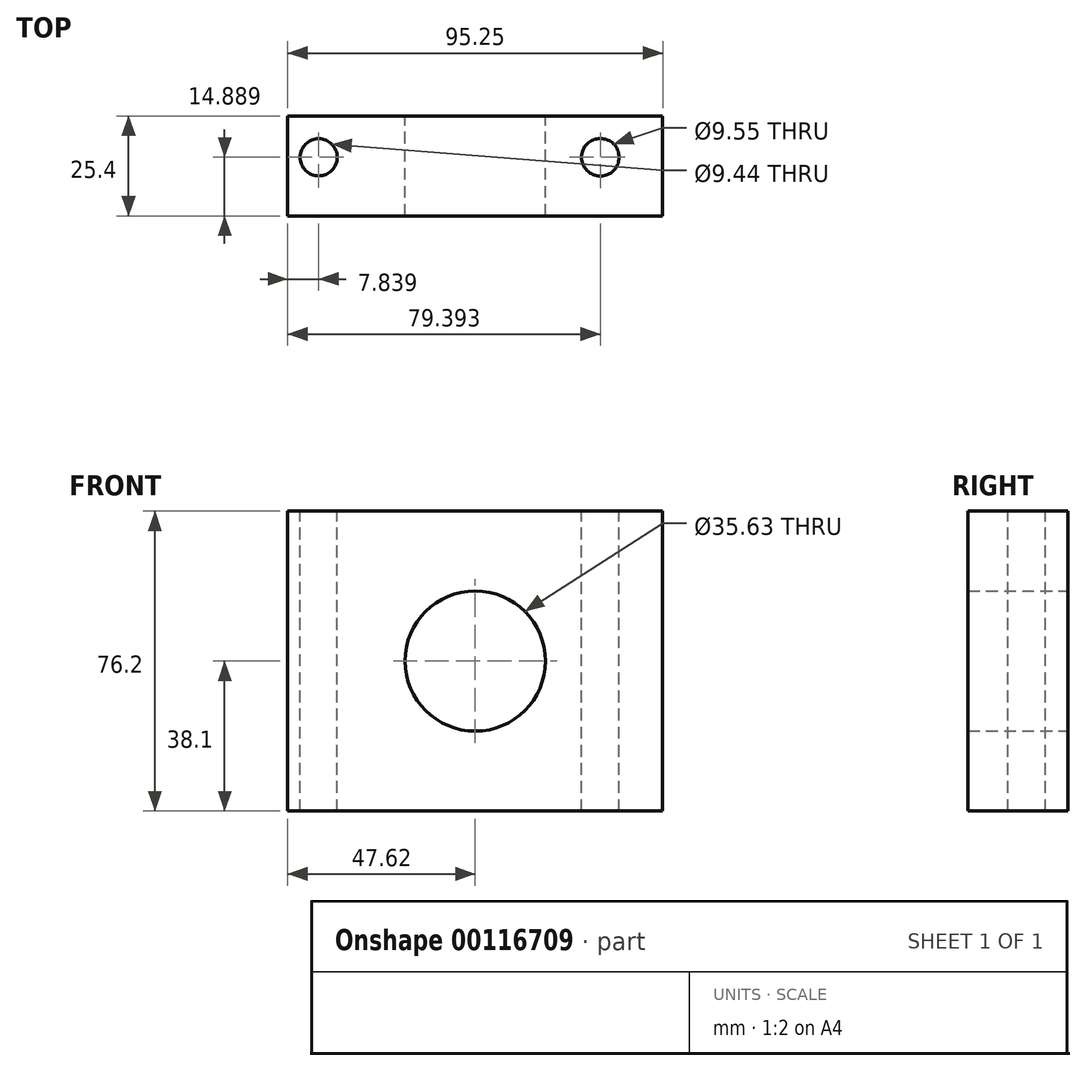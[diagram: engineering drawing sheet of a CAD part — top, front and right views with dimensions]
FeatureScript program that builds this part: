
annotation { "Feature Type Name" : "Feature", "Feature Type Description" : "" }
export const myFeature = defineFeature(function(context is Context, id is Id, definition is map)
    precondition{}
    {
        {
            var Q0;
            Q0=qCreatedBy(makeId("Front.planeOp"),FACE);
            var sketch = newSketch(context, id + "F0", { "sketchPlane" : qUnion([Q0])});
            skLineSegment(sketch, "E0.bottom", {"start": v(-37.55, 38.1) * mm, "end": v(57.7, 38.1) * mm});
            skLineSegment(sketch, "E0.top", {"start": v(-37.55, -38.1) * mm, "end": v(57.7, -38.1) * mm});
            skLineSegment(sketch, "E0.left", {"start": v(-37.55, 38.1) * mm, "end": v(-37.55, -38.1) * mm});
            skLineSegment(sketch, "E0.right", {"start": v(57.7, 38.1) * mm, "end": v(57.7, -38.1) * mm});
            skCircle(sketch, "E1", {"center": v(10.07, 0) * mm, "radius": 17.81 * mm});
            skSolve(sketch);
        }
        {
            var Q0;
            Q0=makeQuery(id+"F0.imprint","IMPRINT",FACE,{"disambiguationData":[TD([[makeQuery(id+"F0.imprint","IMPRINT",EDGE,{"derivedFrom":sQuery(id+"F0.wireOp",EDGE,"E0.bottom")}),-1.0]])]});
            extrude(context, id + "F1", {"entities" : qUnion([Q0]), "depth" : 25.4 * mm});
        }
        {
            var Q0;
            Q0=makeQuery(id+"F1.opExtrude","SWEPT_FACE",FACE,{"disambiguationData":[OSD([sQuery(id+"F0.wireOp",EDGE,"E0.bottom")])]});
            var sketch = newSketch(context, id + "F2", { "sketchPlane" : qUnion([Q0])});
            skCircle(sketch, "E2", {"center": v(-29.71, -10.51) * mm, "radius": 4.72 * mm});
            skCircle(sketch, "E3", {"center": v(41.84, -10.51) * mm, "radius": 4.78 * mm});
            skSolve(sketch);
        }
        {
            var Q0;
            Q0 = qSketchRegion(id + "F2", true);
            extrude(context, id + "F3", {"entities" : qUnion([Q0]), "operationType" : NewBodyOperationType.REMOVE, "oppositeDirection" : true, "depth" : 254 * mm});
        }
        {
            var Q0;
            Q0 = qSketchRegion(id + "F2", true);
            extrude(context, id + "F4", {"entities" : qUnion([Q0]), "operationType" : NewBodyOperationType.REMOVE, "oppositeDirection" : true, "depth" : 254 * mm});
        }
    });
